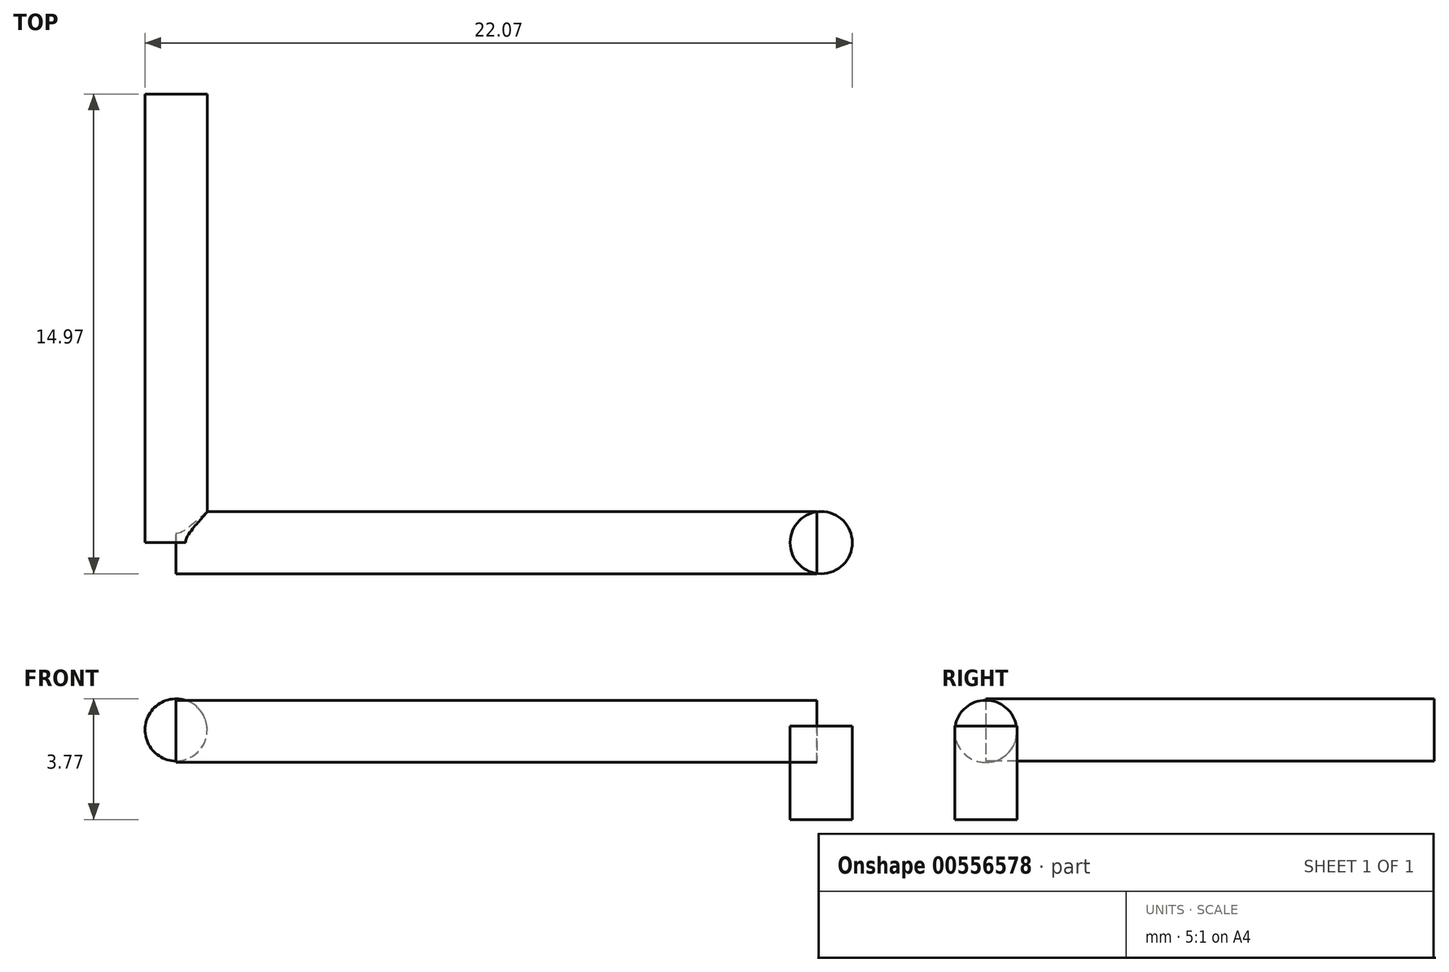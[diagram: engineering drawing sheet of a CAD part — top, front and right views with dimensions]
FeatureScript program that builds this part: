
annotation { "Feature Type Name" : "Feature", "Feature Type Description" : "" }
export const myFeature = defineFeature(function(context is Context, id is Id, definition is map)
    precondition{}
    {
        {
            var Q0;
            Q0=qCreatedBy(makeId("Right.planeOp"),FACE);
            var sketch = newSketch(context, id + "F0", { "sketchPlane" : qUnion([Q0])});
            skCircle(sketch, "E0", {"center": v(0, 1.94) * mm, "radius": 0.97 * mm});
            skSolve(sketch);
        }
        {
            var Q0;
            Q0=makeQuery(id+"F0.imprint","IMPRINT",FACE,{"disambiguationData":[TD([[makeQuery(id+"F0.imprint","IMPRINT",EDGE,{"derivedFrom":sQuery(id+"F0.wireOp",EDGE,"E0")}),1.0]])]});
            extrude(context, id + "F1", {"entities" : qUnion([Q0]), "depth" : 20 * mm, "offsetDistance" : 25 * mm});
        }
        {
            var Q0;
            Q0=qCreatedBy(makeId("Front.planeOp"),FACE);
            var sketch = newSketch(context, id + "F2", { "sketchPlane" : qUnion([Q0])});
            skCircle(sketch, "E1", {"center": v(0, 1.99) * mm, "radius": 0.97 * mm});
            skSolve(sketch);
        }
        {
            var Q0;
            Q0=qSketchRegion(id+"F2",true);
            extrude(context, id + "F3", {"entities" : qUnion([Q0]), "operationType" : NewBodyOperationType.ADD, "depth" : -14 * mm, "offsetDistance" : 25 * mm});
        }
        {
            var Q0;
            Q0=qCreatedBy(makeId("Top.planeOp"),FACE);
            var sketch = newSketch(context, id + "F4", { "sketchPlane" : qUnion([Q0])});
            skCircle(sketch, "E2", {"center": v(14.02, 0) * mm, "radius": 0.97 * mm});
            skSolve(sketch);
        }
        {
            var Q0;
            Q0=makeQuery(id+"F4.imprint","IMPRINT",FACE,{"disambiguationData":[TD([[makeQuery(id+"F4.imprint","IMPRINT",EDGE,{"derivedFrom":sQuery(id+"F4.wireOp",EDGE,"E2")}),1.0]])]});
            extrude(context, id + "F5", {"entities" : qUnion([Q0]), "depth" : -2.91 * mm, "offsetDistance" : 25 * mm});
        }
        {
            var Q0;
            Q0=makeQuery(id+"F5.opExtrude","SWEPT_BODY",BODY,{"disambiguationData":[OSD([sQuery(id+"F4.wireOp",EDGE,"E2")])]});
            transform(context, id + "F6", {"entities" : qUnion([Q0]), "transformType" : TransformType.TRANSLATION_3D, "dx" : 6.11 * mm, "dy" : 0 * mm, "dz" : 2.1 * mm, "makeCopy" : false});
        }
    });
